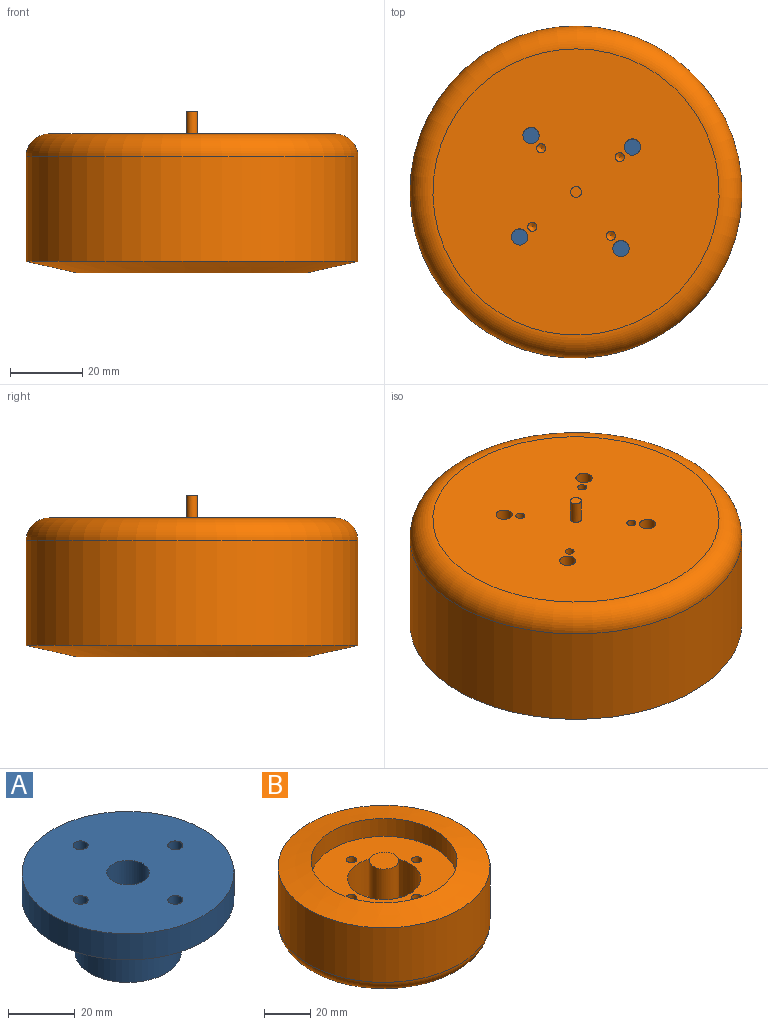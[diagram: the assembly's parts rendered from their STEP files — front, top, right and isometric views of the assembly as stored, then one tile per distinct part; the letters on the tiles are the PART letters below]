
ASSEMBLY  parts=2 mates=1
PART A: 10 faces, bbox 63.4x63.4x29 mm
  f0: plane 63.36x63.36mm, normal (0,0,1), area 2962.4mm2, adj f1,f5,f6,f7,f8,f9
  f1: cylinder r=31.68mm len=63.36mm, axis (0,0,1), area 1895.9mm2, adj f0,f2
  f2: plane 63.36x63.36mm, normal (0,0,-1), area 2297.3mm2, adj f1,f3,f6,f7,f8,f9
  f3: cylinder r=15.88mm len=31.75mm, axis (0,0,1), area 1940.1mm2, adj f2,f4
  f4: plane 31.75x31.75mm, normal (0,0,-1), area 665.1mm2, adj f3,f5
  f5: cylinder r=6.35mm len=28.98mm, axis (0,0,1), area 1156.1mm2, adj f0,f4
  f6: cylinder r=2.25mm len=9.53mm, axis (0,0,1), area 134.7mm2, adj f0,f2
  f7: cylinder r=2.25mm len=9.53mm, axis (0,0,1), area 134.7mm2, adj f0,f2
  f8: cylinder r=2.25mm len=9.53mm, axis (0,0,1), area 134.7mm2, adj f0,f2
  f9: cylinder r=2.25mm len=9.53mm, axis (0,0,1), area 134.7mm2, adj f0,f2
PART B: 24 faces, bbox 99.6x99.6x44.9 mm
  f0: cone r=0mm half-angle=59deg, axis (0,0,-1), area 5.7mm2, adj f1
  f1: cylinder r=1.25mm len=7.85mm, axis (0,0,-1), area 61.7mm2, adj f0,f15
  f2: cone r=0mm half-angle=59deg, axis (0,0,-1), area 5.7mm2, adj f3
  f3: cylinder r=1.25mm len=7.85mm, axis (0,0,-1), area 61.7mm2, adj f2,f15
  f4: cone r=0mm half-angle=59deg, axis (0,0,-1), area 5.7mm2, adj f5
  f5: cylinder r=1.25mm len=7.85mm, axis (0,0,-1), area 61.7mm2, adj f4,f15
  f6: plane 12.7x12.7mm, normal (0,0,1), area 126.7mm2, adj f7
  f7: cylinder r=6.35mm len=28.98mm, axis (0,0,1), area 1156.1mm2, adj f6,f8
  f8: plane 31.75x31.75mm, normal (0,0,1), area 665.1mm2, adj f7,f9
  f9: cylinder r=15.88mm len=31.75mm, axis (0,0,1), area 1940.1mm2, adj f8,f10
  f10: plane 63.36x63.36mm, normal (0,0,1), area 2297.3mm2, adj f9,f11,f20,f21,f22,f23
  f11: cylinder r=31.68mm len=63.36mm, axis (0,0,1), area 1895.9mm2, adj f10,f12
  f12: cone r=46mm half-angle=77.5deg, axis (0,0,-1), area 3579.8mm2, adj f11,f13
  f13: cylinder r=46mm len=92mm, axis (0,0,1), area 8374.5mm2, adj f12,f14
  f14: torus R=39.65mm, axis (0,0,1), area 2738.3mm2, adj f13,f15
  f15: plane 79.3x79.3mm, normal (0,0,-1), area 4848.6mm2, adj f1,f3,f5,f14,f17,f18,f20,f21
  f16: cone r=0mm half-angle=59deg, axis (0,0,-1), area 5.7mm2, adj f17
  f17: cylinder r=1.25mm len=7.85mm, axis (0,0,-1), area 61.7mm2, adj f15,f16
  f18: cylinder r=1.5mm len=6.35mm, axis (0,0,1), area 59.8mm2, adj f15,f19
  f19: plane 3x3mm, normal (0,0,-1), area 7.1mm2, adj f18
  f20: cylinder r=2.25mm len=28.98mm, axis (0,0,1), area 409.6mm2, adj f10,f15
  f21: cylinder r=2.25mm len=28.98mm, axis (0,0,1), area 409.6mm2, adj f10,f15
  f22: cylinder r=2.25mm len=28.98mm, axis (0,0,1), area 409.6mm2, adj f10,f15
  f23: cylinder r=2.25mm len=28.98mm, axis (0,0,1), area 409.6mm2, adj f10,f15
PLACE A rot(axis=(1,0,0),180deg) t=(0,0,38.5)mm
PLACE B rot(axis=(0.9,-0.43,0),180deg) t=(0,0,38.5)mm
MATE revolute B.f7 <-> A.f1  axis (0,0,-1) through (0,0,0)mm
